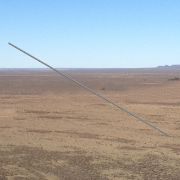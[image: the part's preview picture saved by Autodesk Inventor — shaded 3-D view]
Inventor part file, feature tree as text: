
AUTODESK INVENTOR PART (.ipt)
format: ipt  version: 2014 SP1 (Build 180222100, 222)  size: 125,952 bytes
history: native  units: in
note: dims shown in document units (in); Inventor stores cm internally (conversion verified against a paired STEP export)
features: sketch x2, sweep x1
ambient origin geometry x8: Origin, YZ Plane, XZ Plane, XY Plane, X Axis, Y Axis, Z Axis, Center Point
bodies: Solid1 (feature_tree)
feature tree (3):
  sweep  "Sweep1"
  sketch  "Sketch1"  dims[d0=3.937in d1=0.175in]
  sketch  "Sketch2"  dims[d5=0.0in d6=590.0in]
